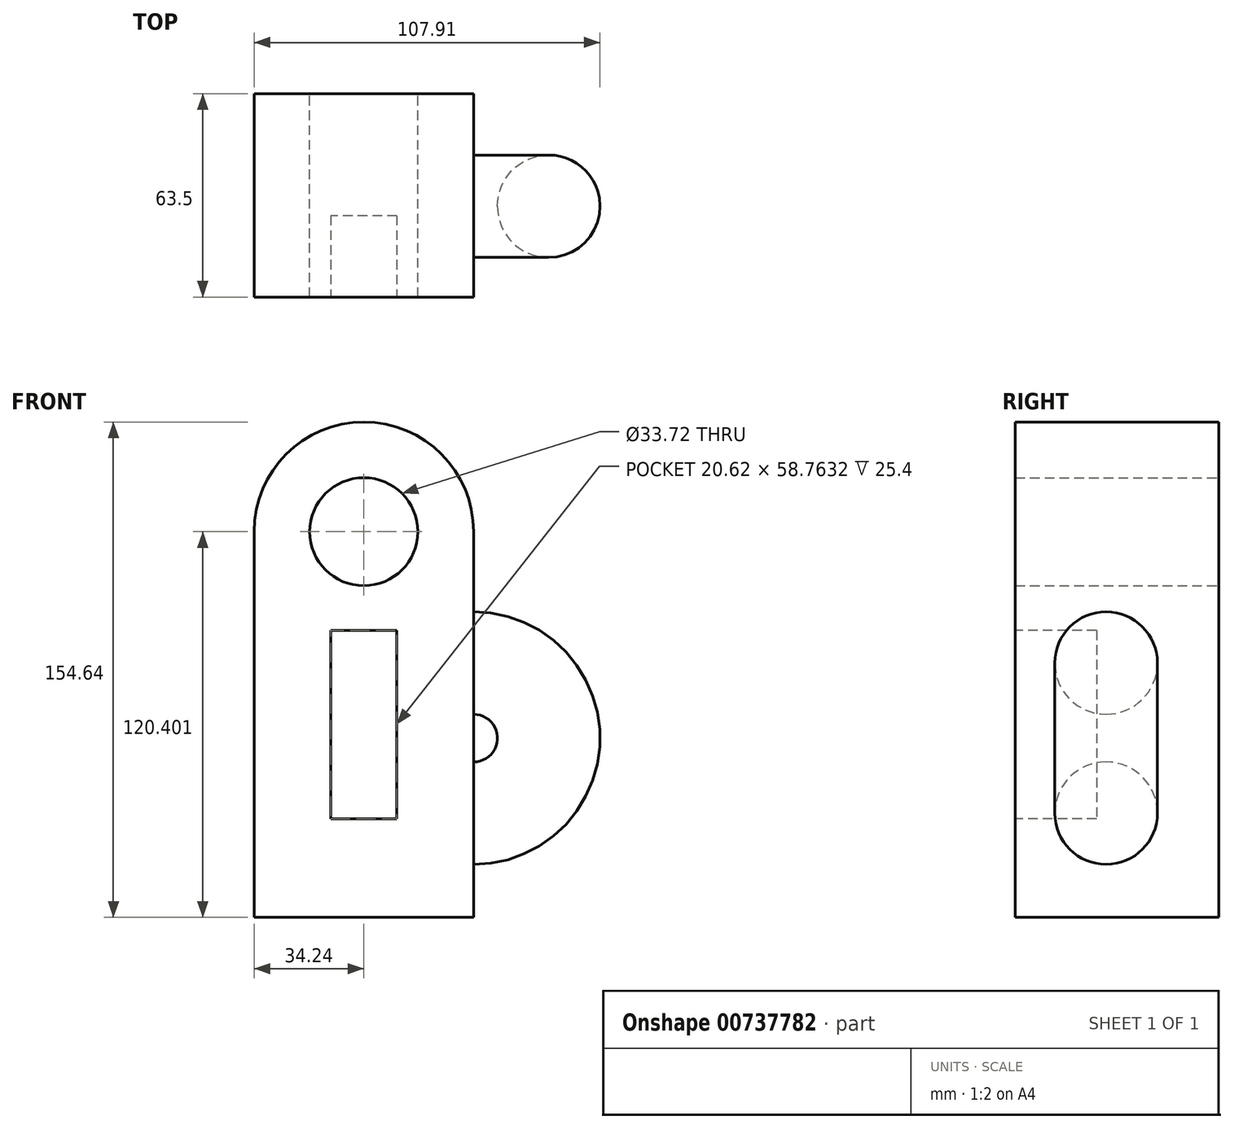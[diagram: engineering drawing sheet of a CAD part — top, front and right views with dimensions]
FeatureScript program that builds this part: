
annotation { "Feature Type Name" : "Feature", "Feature Type Description" : "" }
export const myFeature = defineFeature(function(context is Context, id is Id, definition is map)
    precondition{}
    {
        {
            var Q0;
            Q0=qCreatedBy(makeId("Front.planeOp"),FACE);
            var sketch = newSketch(context, id + "F0", { "sketchPlane" : qUnion([Q0])});
            skLineSegment(sketch, "E0.top", {"start": v(34.24, -60.2) * mm, "end": v(-34.24, -60.2) * mm});
            skLineSegment(sketch, "E0.left", {"start": v(34.24, 60.2) * mm, "end": v(34.24, -60.2) * mm});
            skLineSegment(sketch, "E0.right", {"start": v(-34.24, 60.2) * mm, "end": v(-34.24, -60.2) * mm});
            skPoint(sketch, "E0.middle", {"position": v(0, 0) * mm});
            skArc(sketch, "E1", {"start": v(34.24, 60.2) * mm, "mid": v(0, 94.44) * mm, "end": v(-34.24, 60.2) * mm});
            skCircle(sketch, "E2", {"center": v(0, 60.2) * mm, "radius": 16.86 * mm});
            skSolve(sketch);
        }
        {
            var Q0;
            Q0=makeQuery(id+"F0.imprint","IMPRINT",FACE,{"disambiguationData":[TD([[makeQuery(id+"F0.imprint","IMPRINT",EDGE,{"derivedFrom":sQuery(id+"F0.wireOp",EDGE,"E0.top")}),-1.0]])]});
            extrude(context, id + "F1", {"entities" : qUnion([Q0]), "depth" : 63.5 * mm, "offsetDistance" : 25.4 * mm});
        }
        {
            var Q0;
            Q0=makeQuery(id+"F1.opExtrude","CAP_FACE",FACE,{"disambiguationData":[OSD([sQuery(id+"F0.wireOp",EDGE,"E0.top"),sQuery(id+"F0.wireOp",EDGE,"E0.left"),sQuery(id+"F0.wireOp",EDGE,"E0.right"),sQuery(id+"F0.wireOp",EDGE,"E1"),sQuery(id+"F0.wireOp",EDGE,"E2")])],"isStart":false});
            var sketch = newSketch(context, id + "F2", { "sketchPlane" : qUnion([Q0])});
            skLineSegment(sketch, "E3.bottom", {"start": v(10.3, 29.38) * mm, "end": v(-10.3, 29.38) * mm});
            skLineSegment(sketch, "E3.top", {"start": v(10.3, -29.38) * mm, "end": v(-10.3, -29.38) * mm});
            skLineSegment(sketch, "E3.left", {"start": v(10.3, 29.38) * mm, "end": v(10.3, -29.38) * mm});
            skLineSegment(sketch, "E3.right", {"start": v(-10.3, 29.38) * mm, "end": v(-10.3, -29.38) * mm});
            skPoint(sketch, "E3.middle", {"position": v(0, 0) * mm});
            skSolve(sketch);
        }
        {
            var Q0;
            Q0=makeQuery(id+"F2.imprint","IMPRINT",FACE,{"disambiguationData":[TD([[makeQuery(id+"F2.imprint","IMPRINT",EDGE,{"derivedFrom":sQuery(id+"F2.wireOp",EDGE,"E3.bottom")}),1.0]])]});
            extrude(context, id + "F3", {"entities" : qUnion([Q0]), "operationType" : NewBodyOperationType.REMOVE, "oppositeDirection" : true, "depth" : 25.4 * mm, "offsetDistance" : 25.4 * mm});
        }
        {
            var Q0;
            Q0=makeQuery(id+"F1.opExtrude","SWEPT_FACE",FACE,{"disambiguationData":[OSD([sQuery(id+"F0.wireOp",EDGE,"E0.left")])]});
            var sketch = newSketch(context, id + "F4", { "sketchPlane" : qUnion([Q0])});
            skCircle(sketch, "E4", {"center": v(-35.15, 19.2) * mm, "radius": 16 * mm});
            skLineSegment(sketch, "E5", {"start": v(-63.5, -4.22) * mm, "end": v(0, -4.22) * mm});
            skSolve(sketch);
        }
        {
            var Q0;
            Q0=makeQuery(id+"F4.imprint","IMPRINT",FACE,{"disambiguationData":[TD([[makeQuery(id+"F4.imprint","IMPRINT",EDGE,{"derivedFrom":sQuery(id+"F4.wireOp",EDGE,"E4")}),-1.0]])]});
            var sketch = newSketch(context, id + "F5", { "sketchPlane" : qUnion([Q0])});
            skSolve(sketch);
        }
        {
            var Q0;
            Q0=makeQuery(id+"F5.imprint","IMPRINT",FACE,{"disambiguationData":[TD([[makeQuery(id+"F5.imprint","IMPRINT",EDGE,{"derivedFrom":makeQuery(id+"F4.imprint","IMPRINT",EDGE,{"derivedFrom":sQuery(id+"F4.wireOp",EDGE,"E4")})}),1.0]])]});
            var Q1;
            Q1=sQuery(id+"F4.wireOp",EDGE,"E5");
            revolve(context, id + "F6", {"operationType" : NewBodyOperationType.ADD, "surfaceOperationType" : NewSurfaceOperationType.NEW, "entities" : qUnion([Q0]), "axis" : qUnion([Q1]), "revolveType" : RevolveType.ONE_DIRECTION, "angle" : 180 * degree});
        }
    });
